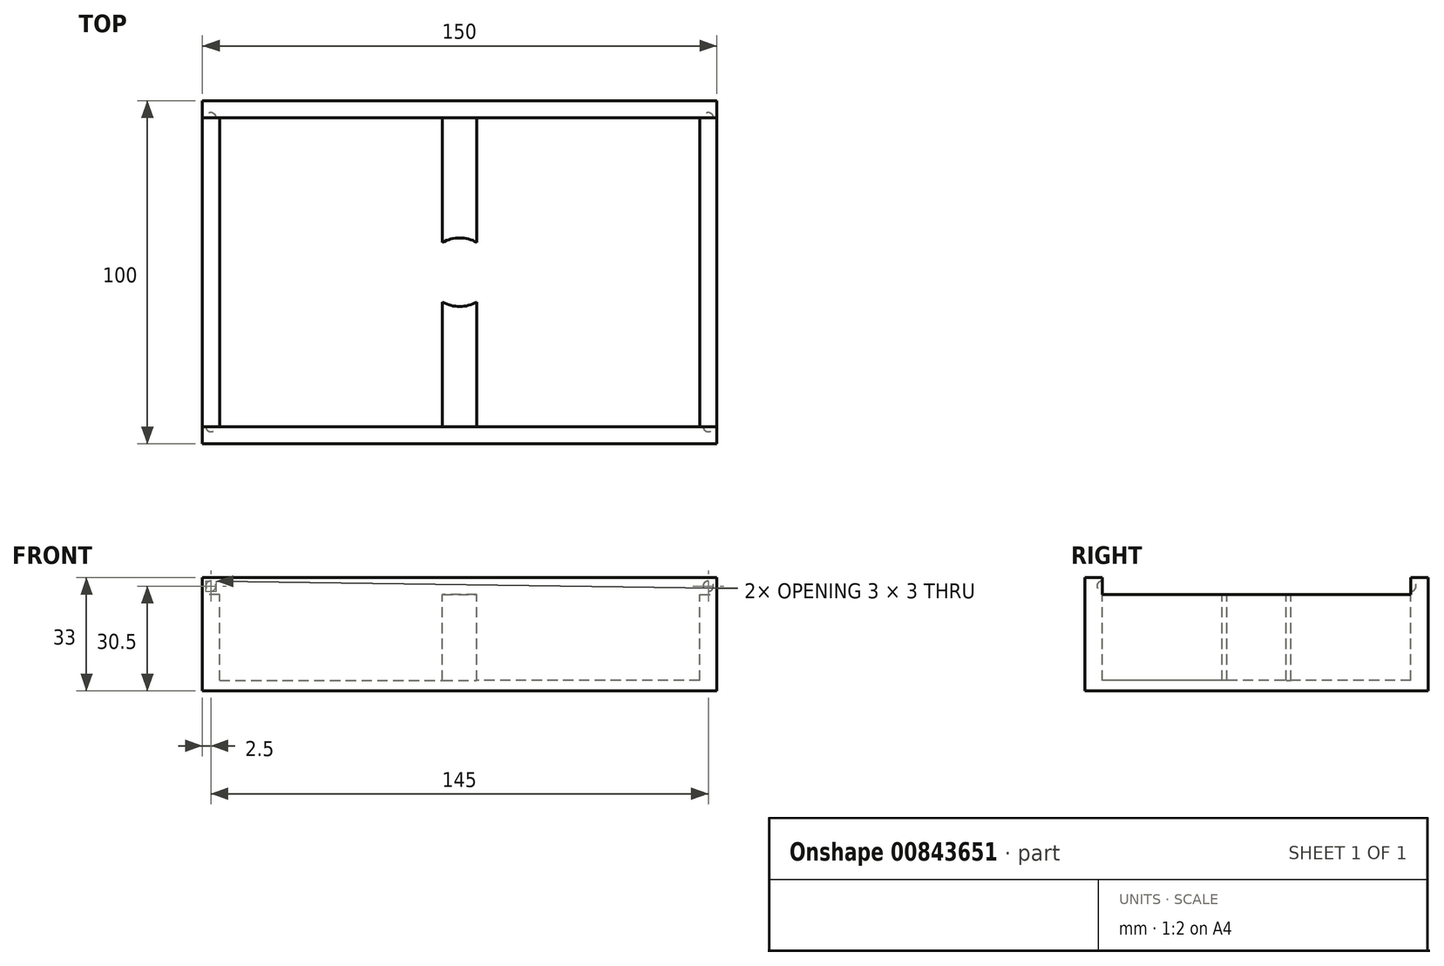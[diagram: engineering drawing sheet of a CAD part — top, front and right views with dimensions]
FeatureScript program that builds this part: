
annotation { "Feature Type Name" : "Feature", "Feature Type Description" : "" }
export const myFeature = defineFeature(function(context is Context, id is Id, definition is map)
    precondition{}
    {
        {
            var Q0;
            Q0=qCreatedBy(makeId("Top.planeOp"),FACE);
            var sketch = newSketch(context, id + "F0", { "sketchPlane" : qUnion([Q0])});
            skLineSegment(sketch, "E0.bottom", {"start": v(75, -50) * mm, "end": v(-75, -50) * mm});
            skLineSegment(sketch, "E0.top", {"start": v(75, 50) * mm, "end": v(-75, 50) * mm});
            skLineSegment(sketch, "E0.left", {"start": v(75, -50) * mm, "end": v(75, 50) * mm});
            skLineSegment(sketch, "E0.right", {"start": v(-75, -50) * mm, "end": v(-75, 50) * mm});
            skPoint(sketch, "E0.middle", {"position": v(0, 0) * mm});
            skSolve(sketch);
        }
        {
            var Q0;
            Q0 = qSketchRegion(id + "F0", true);
            extrude(context, id + "F1", {"entities" : qUnion([Q0]), "depth" : 33 * mm, "offsetDistance" : 25 * mm});
        }
        {
            var Q0;
            Q0=makeQuery(id+"F1.opExtrude","CAP_FACE",FACE,{"disambiguationData":[OSD([sQuery(id+"F0.wireOp",EDGE,"E0.bottom"),sQuery(id+"F0.wireOp",EDGE,"E0.top"),sQuery(id+"F0.wireOp",EDGE,"E0.left"),sQuery(id+"F0.wireOp",EDGE,"E0.right")])],"isStart":false});
            var sketch = newSketch(context, id + "F2", { "sketchPlane" : qUnion([Q0])});
            skLineSegment(sketch, "E1.bottom", {"start": v(-70, 45) * mm, "end": v(-5, 45) * mm});
            skLineSegment(sketch, "E1.top", {"start": v(-70, -45) * mm, "end": v(-5, -45) * mm});
            skLineSegment(sketch, "E1.left", {"start": v(-70, 45) * mm, "end": v(-70, -45) * mm});
            skLineSegment(sketch, "E1.right", {"start": v(-5, 45) * mm, "end": v(-5, -45) * mm});
            skPoint(sketch, "E1.middle", {"position": v(-37.5, 0) * mm});
            skPoint(sketch, "E2", {"position": v(0, 50) * mm});
            skPoint(sketch, "E3", {"position": v(-37.5, 50) * mm});
            skLineSegment(sketch, "E4.MirrorCS", {"start": v(70, 45) * mm, "end": v(70, -45) * mm});
            skLineSegment(sketch, "E5.MirrorCS", {"start": v(70, -45) * mm, "end": v(5, -45) * mm});
            skLineSegment(sketch, "E6.MirrorCS", {"start": v(70, 45) * mm, "end": v(5, 45) * mm});
            skLineSegment(sketch, "E7.MirrorCS", {"start": v(5, 45) * mm, "end": v(5, -45) * mm});
            skSolve(sketch);
        }
        {
            var Q0;
            Q0=makeQuery(id+"F2.imprint","IMPRINT",FACE,{"disambiguationData":[TD([[makeQuery(id+"F2.imprint","IMPRINT",EDGE,{"derivedFrom":sQuery(id+"F2.wireOp",EDGE,"E1.bottom")}),-1.0]])]});
            var Q1;
            Q1=makeQuery(id+"F2.imprint","IMPRINT",FACE,{"disambiguationData":[TD([[makeQuery(id+"F2.imprint","IMPRINT",EDGE,{"derivedFrom":sQuery(id+"F2.wireOp",EDGE,"E4.MirrorCS")}),-1.0]])]});
            extrude(context, id + "F3", {"entities" : qUnion([Q0, Q1]), "operationType" : NewBodyOperationType.REMOVE, "oppositeDirection" : true, "depth" : 30 * mm, "offsetDistance" : 25 * mm});
        }
        {
            var Q0;
            Q0=makeQuery(id+"F1.opExtrude","CAP_FACE",FACE,{"disambiguationData":[OSD([sQuery(id+"F0.wireOp",EDGE,"E0.bottom"),sQuery(id+"F0.wireOp",EDGE,"E0.top"),sQuery(id+"F0.wireOp",EDGE,"E0.left"),sQuery(id+"F0.wireOp",EDGE,"E0.right")])],"isStart":false});
            var sketch = newSketch(context, id + "F4", { "sketchPlane" : qUnion([Q0])});
            skLineSegment(sketch, "E8.bottom", {"start": v(-70, 45) * mm, "end": v(-75, 45) * mm});
            skLineSegment(sketch, "E8.top", {"start": v(-70, -45) * mm, "end": v(-75, -45) * mm});
            skLineSegment(sketch, "E8.left", {"start": v(-70, 45) * mm, "end": v(-70, -45) * mm});
            skLineSegment(sketch, "E8.right", {"start": v(-75, 45) * mm, "end": v(-75, -45) * mm});
            skLineSegment(sketch, "E9.bottom", {"start": v(-5, 45) * mm, "end": v(0, 45) * mm});
            skLineSegment(sketch, "E9.top", {"start": v(-5, -45) * mm, "end": v(0, -45) * mm});
            skLineSegment(sketch, "E9.left", {"start": v(-5, 45) * mm, "end": v(-5, -45) * mm});
            skLineSegment(sketch, "E9.right", {"start": v(0, 45) * mm, "end": v(0, -45) * mm});
            skLineSegment(sketch, "E10.MirrorCS", {"start": v(70, 45) * mm, "end": v(70, -45) * mm});
            skLineSegment(sketch, "E11.MirrorCS", {"start": v(70, 45) * mm, "end": v(75, 45) * mm});
            skLineSegment(sketch, "E12.MirrorCS", {"start": v(75, 45) * mm, "end": v(75, -45) * mm});
            skLineSegment(sketch, "E13.MirrorCS", {"start": v(70, -45) * mm, "end": v(75, -45) * mm});
            skLineSegment(sketch, "E14.MirrorCS", {"start": v(5, 45) * mm, "end": v(5, -45) * mm});
            skLineSegment(sketch, "E15.MirrorCS", {"start": v(5, -45) * mm, "end": v(0, -45) * mm});
            skLineSegment(sketch, "E16.MirrorCS", {"start": v(5, 45) * mm, "end": v(0, 45) * mm});
            skSolve(sketch);
        }
        {
            var Q0;
            Q0 = qSketchRegion(id + "F4", true);
            extrude(context, id + "F5", {"entities" : qUnion([Q0]), "operationType" : NewBodyOperationType.REMOVE, "oppositeDirection" : true, "depth" : 5 * mm, "offsetDistance" : 25 * mm});
        }
        {
            var Q0;
            Q0=makeQuery(id+"F5.boolean.opBoolean","MERGE",FACE,{"derivedFrom":[makeQuery(id+"F3.boolean.opBoolean","COPY",FACE,{"derivedFrom":makeQuery(id+"F3.opExtrude","SWEPT_FACE",FACE,{"disambiguationData":[OSD([sQuery(id+"F2.wireOp",EDGE,"E1.bottom")])]})}),makeQuery(id+"F3.boolean.opBoolean","COPY",FACE,{"derivedFrom":makeQuery(id+"F3.opExtrude","SWEPT_FACE",FACE,{"disambiguationData":[OSD([sQuery(id+"F2.wireOp",EDGE,"E6.MirrorCS")])]})}),makeQuery(id+"F5.opExtrude","SWEPT_FACE",FACE,{"disambiguationData":[OSD([sQuery(id+"F4.wireOp",EDGE,"E8.bottom")])]}),makeQuery(id+"F5.opExtrude","SWEPT_FACE",FACE,{"disambiguationData":[OSD([sQuery(id+"F4.wireOp",EDGE,"E9.bottom"),sQuery(id+"F4.wireOp",EDGE,"E16.MirrorCS")])]}),makeQuery(id+"F5.opExtrude","SWEPT_FACE",FACE,{"disambiguationData":[OSD([sQuery(id+"F4.wireOp",EDGE,"E11.MirrorCS")])]})]});
            var sketch = newSketch(context, id + "F6", { "sketchPlane" : qUnion([Q0])});
            skPoint(sketch, "E17", {"position": v(-72.5, 30.5) * mm});
            skArc(sketch, "E18", {"start": v(-72.5, 32) * mm, "mid": v(-74, 30.5) * mm, "end": v(-72.5, 29) * mm});
            skLineSegment(sketch, "E19", {"start": v(-72.5, 32) * mm, "end": v(-72.5, 29) * mm});
            skSolve(sketch);
        }
        {
            var Q0;
            Q0=makeQuery(id+"F5.boolean.opBoolean","COPY",FACE,{"derivedFrom":makeQuery(id+"F5.opExtrude","CAP_FACE",FACE,{"disambiguationData":[OSD([sQuery(id+"F4.wireOp",EDGE,"E9.bottom"),sQuery(id+"F4.wireOp",EDGE,"E9.top"),sQuery(id+"F4.wireOp",EDGE,"E9.left"),sQuery(id+"F4.wireOp",EDGE,"E14.MirrorCS"),sQuery(id+"F4.wireOp",EDGE,"E15.MirrorCS"),sQuery(id+"F4.wireOp",EDGE,"E16.MirrorCS")])],"isStart":false})});
            var sketch = newSketch(context, id + "F7", { "sketchPlane" : qUnion([Q0])});
            skCircle(sketch, "E20", {"center": v(0, 0) * mm, "radius": 10 * mm});
            skSolve(sketch);
        }
        {
            var Q0;
            Q0 = qSketchRegion(id + "F7", true);
            var Q1;
            Q1=makeQuery(id+"F3.boolean.opBoolean","COPY",FACE,{"derivedFrom":makeQuery(id+"F3.opExtrude","CAP_FACE",FACE,{"disambiguationData":[OSD([sQuery(id+"F2.wireOp",EDGE,"E4.MirrorCS"),sQuery(id+"F2.wireOp",EDGE,"E5.MirrorCS"),sQuery(id+"F2.wireOp",EDGE,"E6.MirrorCS"),sQuery(id+"F2.wireOp",EDGE,"E7.MirrorCS")])],"isStart":false})});
            extrude(context, id + "F8", {"entities" : qUnion([Q0]), "operationType" : NewBodyOperationType.REMOVE, "endBound" : BoundingType.UP_TO_SURFACE, "oppositeDirection" : true, "depth" : 25 * mm, "endBoundEntityFace" : qUnion([Q1]), "offsetDistance" : 25 * mm});
        }
        {
            var Q0;
            Q0 = qSketchRegion(id + "F6", true);
            var Q1;
            Q1=sQuery(id+"F6.wireOp",EDGE,"E19");
            revolve(context, id + "F9", {"operationType" : NewBodyOperationType.REMOVE, "surfaceOperationType" : NewSurfaceOperationType.NEW, "entities" : qUnion([Q0]), "axis" : qUnion([Q1]), "revolveType" : RevolveType.FULL, "oppositeDirection" : true});
        }
        {
            var Q0;
            Q0=makeQuery(id+"F1.opExtrude","SWEPT_BODY",BODY,{"disambiguationData":[OSD([sQuery(id+"F0.wireOp",EDGE,"E0.bottom"),sQuery(id+"F0.wireOp",EDGE,"E0.top"),sQuery(id+"F0.wireOp",EDGE,"E0.left"),sQuery(id+"F0.wireOp",EDGE,"E0.right")])]});
            var Q1;
            Q1=qCreatedBy(makeId("Right.planeOp"),FACE);
            mirror(context, id + "F10", {"operationType" : NewBodyOperationType.INTERSECT, "entities" : qUnion([Q0]), "mirrorPlane" : qUnion([Q1])});
        }
        {
            var Q0;
            Q0=makeQuery(id+"F1.opExtrude","SWEPT_BODY",BODY,{"disambiguationData":[OSD([sQuery(id+"F0.wireOp",EDGE,"E0.bottom"),sQuery(id+"F0.wireOp",EDGE,"E0.top"),sQuery(id+"F0.wireOp",EDGE,"E0.left"),sQuery(id+"F0.wireOp",EDGE,"E0.right")])]});
            var Q1;
            Q1=qCreatedBy(makeId("Front.planeOp"),FACE);
            mirror(context, id + "F11", {"operationType" : NewBodyOperationType.INTERSECT, "entities" : qUnion([Q0]), "mirrorPlane" : qUnion([Q1])});
        }
    });
